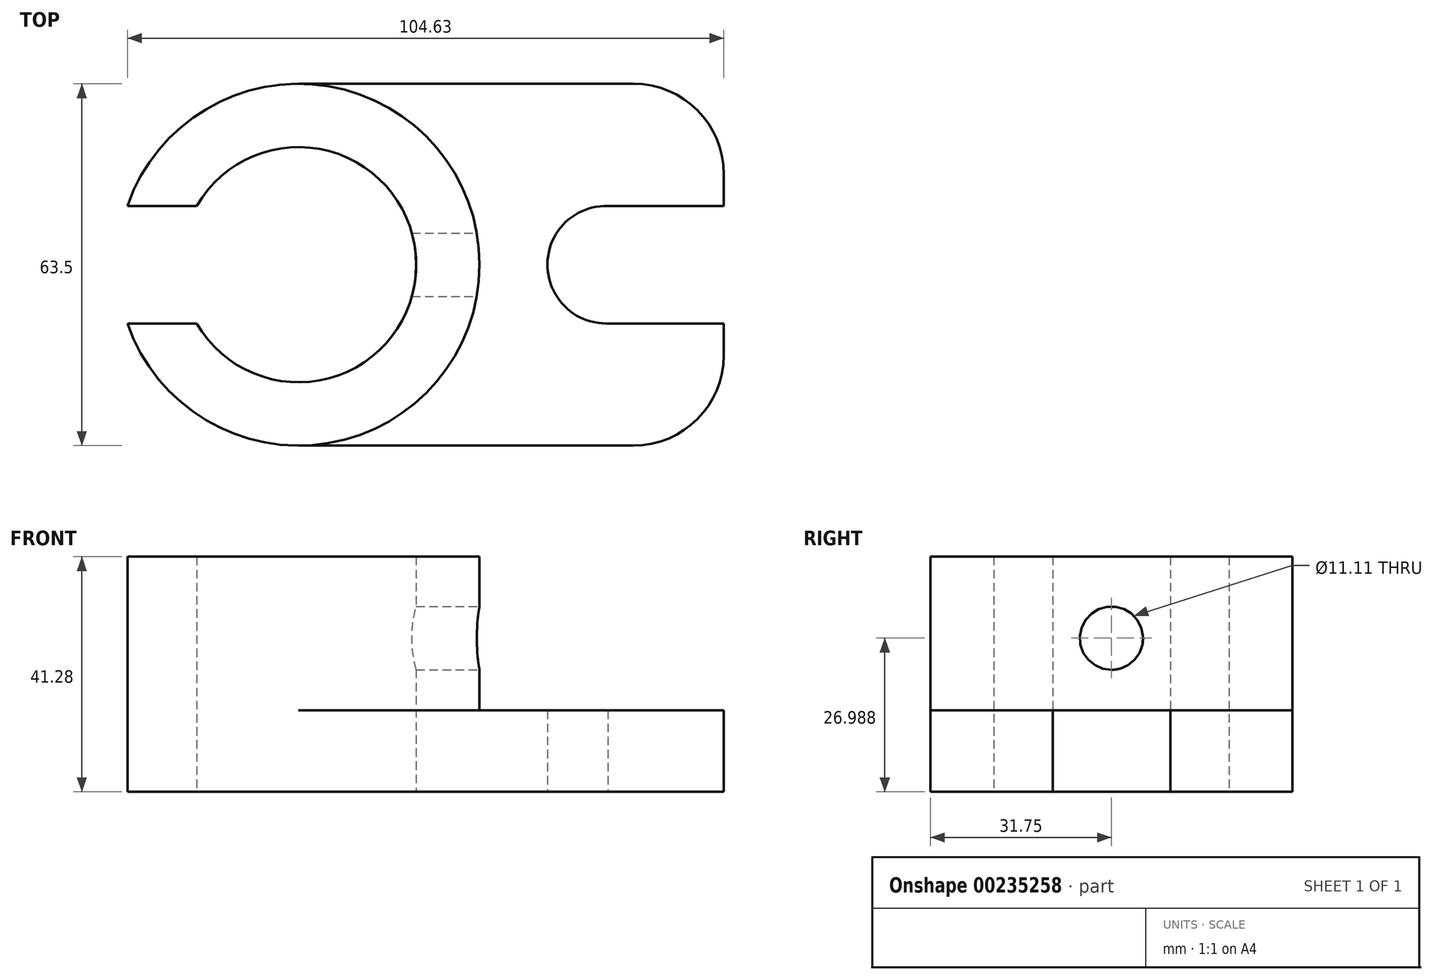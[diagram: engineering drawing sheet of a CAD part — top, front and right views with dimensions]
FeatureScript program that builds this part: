
annotation { "Feature Type Name" : "Feature", "Feature Type Description" : "" }
export const myFeature = defineFeature(function(context is Context, id is Id, definition is map)
    precondition{}
    {
        {
            var Q0;
            Q0=qCreatedBy(makeId("Top.planeOp"),FACE);
            var sketch = newSketch(context, id + "F0", { "sketchPlane" : qUnion([Q0])});
            skLineSegment(sketch, "E0.bottom", {"start": v(-21.44, 31.75) * mm, "end": v(37.3, 31.75) * mm});
            skLineSegment(sketch, "E0.top", {"start": v(-21.44, -31.75) * mm, "end": v(37.3, -31.75) * mm});
            skLineSegment(sketch, "E0.left", {"start": v(-53.19, 0) * mm, "end": v(-53.19, 0) * mm});
            skLineSegment(sketch, "E0.right", {"start": v(53.17, 15.88) * mm, "end": v(53.17, 10.31) * mm});
            skPoint(sketch, "E1.visualSharp", {"position": v(53.17, -31.75) * mm});
            skArc(sketch, "E1.filletArc", {"start": v(37.3, -31.75) * mm, "mid": v(48.53, -27.1) * mm, "end": v(53.17, -15.87) * mm});
            skPoint(sketch, "E2.visualSharp", {"position": v(53.17, 31.75) * mm});
            skArc(sketch, "E2.filletArc", {"start": v(53.17, 15.88) * mm, "mid": v(48.53, 27.1) * mm, "end": v(37.3, 31.75) * mm});
            skPoint(sketch, "E3.visualSharp", {"position": v(-53.19, 31.75) * mm});
            skArc(sketch, "E3.filletArc", {"start": v(-21.44, 31.75) * mm, "mid": v(-39.88, 25.84) * mm, "end": v(-51.46, 10.32) * mm});
            skPoint(sketch, "E4.visualSharp", {"position": v(-53.19, -31.75) * mm});
            skArc(sketch, "E4.filletArc", {"start": v(-51.46, -10.32) * mm, "mid": v(4.4, -18.45) * mm, "end": v(-21.44, 31.75) * mm});
            skLineSegment(sketch, "E5", {"start": v(-51.46, 10.32) * mm, "end": v(-39.31, 10.32) * mm});
            skLineSegment(sketch, "E6", {"start": v(-39.31, -10.32) * mm, "end": v(-51.46, -10.32) * mm});
            skArc(sketch, "E7", {"start": v(-39.31, -10.32) * mm, "mid": v(-0.8, 0) * mm, "end": v(-39.31, 10.32) * mm});
            skArc(sketch, "E8", {"start": v(32.85, 10.31) * mm, "mid": v(22.22, 0.16) * mm, "end": v(32.54, -10.32) * mm});
            skPoint(sketch, "E8.centerSnap0", {"position": v(53.17, 0) * mm});
            skLineSegment(sketch, "E9", {"start": v(32.85, 10.31) * mm, "end": v(53.17, 10.31) * mm});
            skLineSegment(sketch, "E10", {"start": v(32.54, -10.32) * mm, "end": v(53.17, -10.32) * mm});
            skLineSegment(sketch, "E11.trimOffspring", {"start": v(53.17, -10.32) * mm, "end": v(53.17, -15.87) * mm});
            skSolve(sketch);
        }
        {
            var Q0;
            {var subQ1=sQuery(id+"F0.wireOp",EDGE,"E3.filletArc");Q0=makeQuery(id+"F0.imprint","IMPRINT",FACE,{"disambiguationData":[TD([[makeQuery(id+"F0.imprint","IMPRINT",EDGE,{"derivedFrom":subQ1}),1.0]])]});}
            extrude(context, id + "F1", {"entities" : qUnion([Q0]), "depth" : 41.27 * mm});
        }
        {
            var Q0;
            Q0 = qSketchRegion(id + "F0", true);
            extrude(context, id + "F2", {"entities" : qUnion([Q0]), "operationType" : NewBodyOperationType.ADD, "depth" : 14.29 * mm});
        }
        {
            var Q0;
            Q0=qCreatedBy(makeId("Right.planeOp"),FACE);
            cPlane(context, id + "F3", {"entities" : qUnion([Q0]), "cplaneType" : CPlaneType.OFFSET, "offset" : 25.4 * mm, "width" : 152.4 * mm, "height" : 152.4 * mm});
        }
        {
            var Q0;
            Q0=qCreatedBy(id+"F3.planeOp",FACE);
            var sketch = newSketch(context, id + "F4", { "sketchPlane" : qUnion([Q0])});
            skCircle(sketch, "E12", {"center": v(0, 26.99) * mm, "radius": 5.56 * mm});
            skSolve(sketch);
        }
        {
            var Q0;
            Q0 = qSketchRegion(id + "F4", true);
            extrude(context, id + "F5", {"entities" : qUnion([Q0]), "operationType" : NewBodyOperationType.REMOVE, "oppositeDirection" : true, "depth" : 38.1 * mm});
        }
    });
